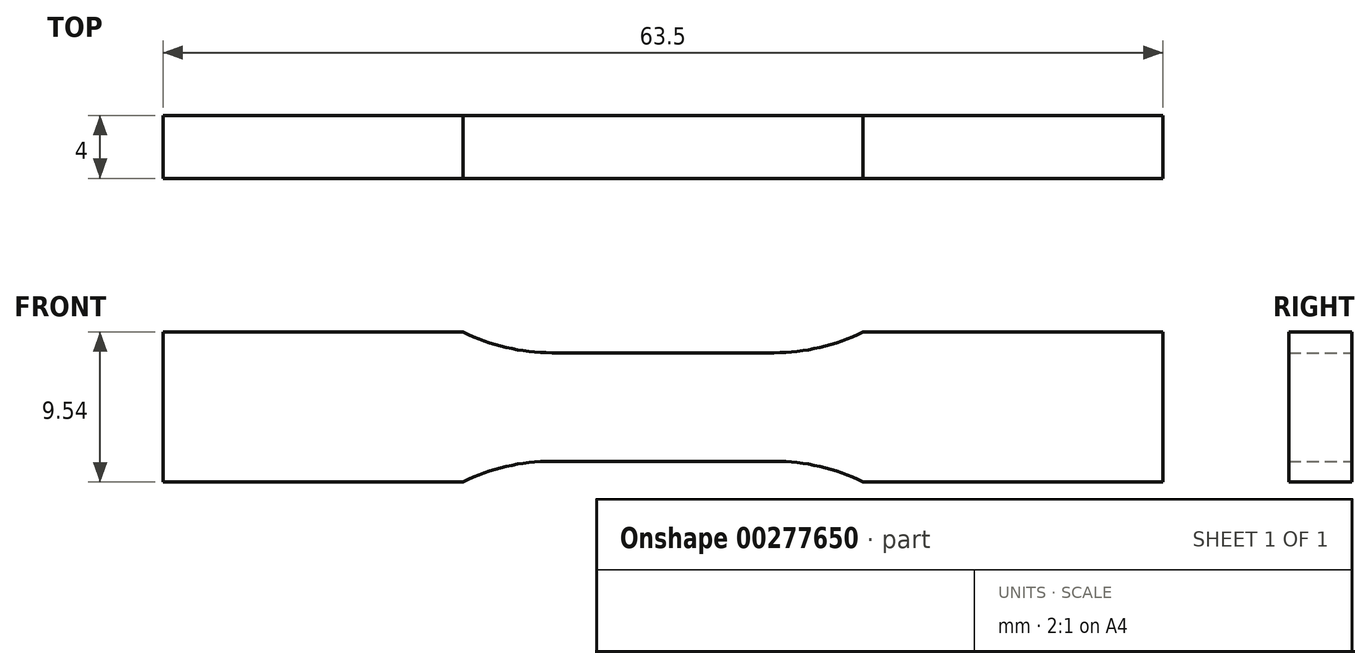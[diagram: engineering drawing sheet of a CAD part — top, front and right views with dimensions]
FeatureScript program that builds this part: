
annotation { "Feature Type Name" : "Feature", "Feature Type Description" : "" }
export const myFeature = defineFeature(function(context is Context, id is Id, definition is map)
    precondition{}
    {
        {
            var Q0;
            Q0=qCreatedBy(makeId("Front.planeOp"),FACE);
            var sketch = newSketch(context, id + "F0", { "sketchPlane" : qUnion([Q0])});
            skLineSegment(sketch, "E0", {"start": v(0, 3.44) * mm, "end": v(7.06, 3.44) * mm});
            skArc(sketch, "E1", {"start": v(7.06, 3.44) * mm, "mid": v(9.96, 3.78) * mm, "end": v(12.7, 4.77) * mm});
            skLineSegment(sketch, "E2", {"start": v(12.7, 4.77) * mm, "end": v(31.75, 4.77) * mm});
            skLineSegment(sketch, "E3.MirrorCS", {"start": v(12.7, -4.77) * mm, "end": v(31.75, -4.77) * mm});
            skLineSegment(sketch, "E4.MirrorCS", {"start": v(0, -3.44) * mm, "end": v(7.06, -3.44) * mm});
            skArc(sketch, "E5.MirrorCS", {"start": v(7.06, -3.44) * mm, "mid": v(9.96, -3.78) * mm, "end": v(12.7, -4.77) * mm});
            skArc(sketch, "E6.MirrorCS", {"start": v(-7.06, -3.44) * mm, "mid": v(-9.96, -3.78) * mm, "end": v(-12.7, -4.77) * mm});
            skLineSegment(sketch, "E7.MirrorCS", {"start": v(0, 3.44) * mm, "end": v(-7.06, 3.44) * mm});
            skArc(sketch, "E8.MirrorCS", {"start": v(-7.06, 3.44) * mm, "mid": v(-9.96, 3.78) * mm, "end": v(-12.7, 4.77) * mm});
            skLineSegment(sketch, "E9.MirrorCS", {"start": v(-12.7, -4.77) * mm, "end": v(-31.75, -4.77) * mm});
            skLineSegment(sketch, "E10.MirrorCS", {"start": v(0, -3.44) * mm, "end": v(-7.06, -3.44) * mm});
            skLineSegment(sketch, "E11.MirrorCS", {"start": v(-12.7, 4.77) * mm, "end": v(-31.75, 4.77) * mm});
            skLineSegment(sketch, "E12", {"start": v(-31.75, 4.77) * mm, "end": v(-31.75, -4.77) * mm});
            skLineSegment(sketch, "E13", {"start": v(31.75, 4.77) * mm, "end": v(31.75, -4.77) * mm});
            skSolve(sketch);
        }
        {
            var Q0;
            Q0 = qSketchRegion(id + "F0", true);
            extrude(context, id + "F1", {"entities" : qUnion([Q0]), "endBound" : BoundingType.SYMMETRIC, "depth" : 4 * mm});
        }
    });
